# Revit family: 55537_Door-HdwrLever-commcl
name_source: partatom
category: Doors
revit_build: Autodesk Revit Architecture 2013 (Build: 20120221_2030(x64)
units: mm (PartAtom-declared; Revit-internal decimal feet)

## types (1)
- 55537_Door-HdwrLever-commcl
    ANSI Conformance = A156.2
    Assembly Code = C1020410
    Construction Details = http://www.arcat.com
    Default Elevation = 1000 mm
    Description = Door Lever
    Door Hardware UL Listed = Yes
    Door Slab Thickness = 40 mm
    Expected Lifespan (Years) = 0
    Function = Interior
    Height = 37 mm
    Keynote = 08710
    Latch Strike Type = Curved Lip
    Lock Cylinder Finish = ARCAT - Metal - Brass, Polished
    Lock Cylinder Pin Count = 6
    Lock Cylinder Type = Conventional
    Maintenance Schedule (Months) = 0
    Manufacturer = Generic
    Manufacturer Fax = (203) 929-2444
    Manufacturer Website = http://www.arcat.com
    Model = Generic
    Product Data = http://www.arcat.com
    Product Properties = http://www.arcat.com
    Specification = http://www.arcat.com
    Thickness = 0 mm  [stored 0 ft]
    Warranty Duration (Years) = 0
    boltloc = 14 mm  [stored 0.0459318 ft]
    ltchloc = 7 mm

note: [stored X ft] marks values corroborated as IEEE doubles in the binary element streams (Revit-internal decimal feet)

## geometry (parser evidence)
native form markers: Sweep x3
no freeform markers — native parametric forms only
